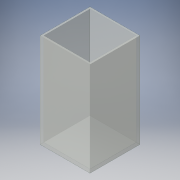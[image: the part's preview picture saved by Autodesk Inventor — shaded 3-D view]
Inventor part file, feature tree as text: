
AUTODESK INVENTOR PART (.ipt)
format: ipt  version: 2016 (Build 200138000, 138)  size: 105,472 bytes
history: native  units: mm
features: extrude x2, sketch x2
ambient origin geometry x8: Origin, YZ Plane, XZ Plane, XY Plane, X Axis, Y Axis, Z Axis, Center Point
bodies: Solid1 (feature_tree)
feature tree (4):
  extrude  "Extrusion1"  Depth=75.0mm
  extrude  "Extrusion2"  Depth=3.0mm
  sketch  "Sketch1"  dims[d0=75.0mm d1=75.0mm]
  sketch  "Sketch2"  dims[d2=3.0mm d3=3.0mm d4=3.0mm d5=3.0mm d6=150.0mm d7=0.0mm d8=3.0mm d9=0.0mm]
